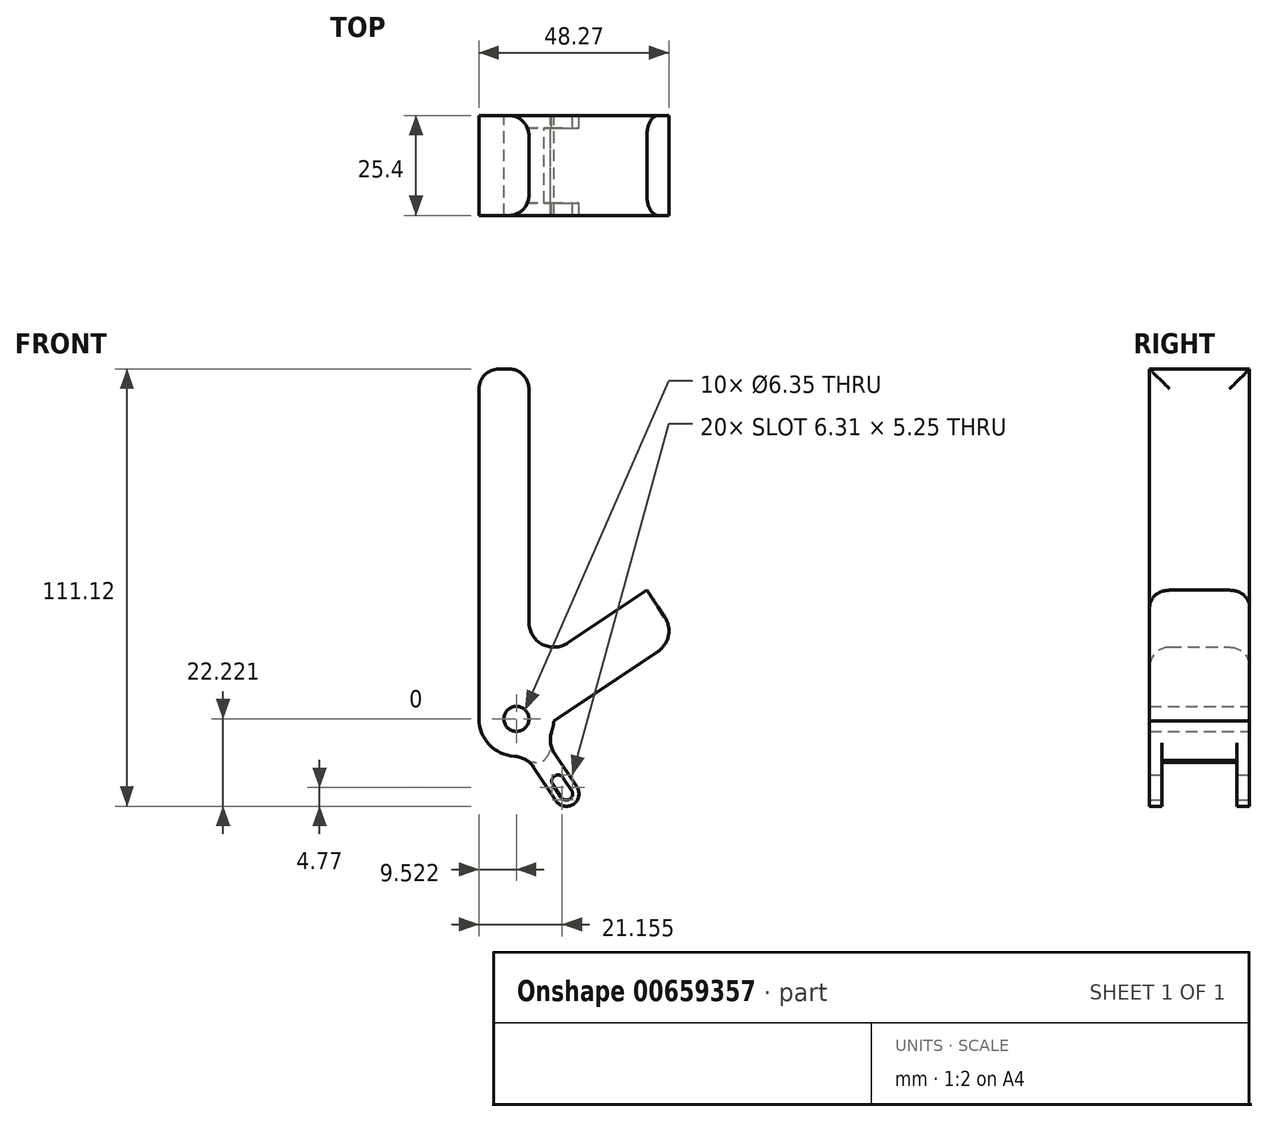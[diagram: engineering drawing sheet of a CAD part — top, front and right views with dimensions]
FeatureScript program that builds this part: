
annotation { "Feature Type Name" : "Feature", "Feature Type Description" : "" }
export const myFeature = defineFeature(function(context is Context, id is Id, definition is map)
    precondition{}
    {
        {
            var Q0;
            Q0=qCreatedBy(makeId("Front.planeOp"),FACE);
            var sketch = newSketch(context, id + "F0", { "sketchPlane" : qUnion([Q0])});
            skPoint(sketch, "E0.centerSnap0", {"position": v(3.9, -22.32) * mm});
            skArc(sketch, "E1", {"start": v(-1.4, -6.47) * mm, "mid": v(-1.04, -5.16) * mm, "end": v(-0.87, -3.81) * mm});
            skArc(sketch, "E2", {"start": v(1, -23.23) * mm, "mid": v(3.2, -23.67) * mm, "end": v(3.64, -21.47) * mm});
            skArc(sketch, "E3", {"start": v(-0.32, -24.11) * mm, "mid": v(4.08, -25) * mm, "end": v(4.96, -20.59) * mm});
            skLineSegment(sketch, "E4", {"start": v(-10.38, -3.3) * mm, "end": v(2.32, -22.35) * mm, "construction": true});
            skArc(sketch, "E5", {"start": v(1.5, -18.27) * mm, "mid": v(-0.7, -17.83) * mm, "end": v(-1.13, -20.03) * mm});
            skLineSegment(sketch, "E6", {"start": v(0.19, -19.15) * mm, "end": v(-1.13, -20.03) * mm, "construction": true});
            skLineSegment(sketch, "E7", {"start": v(0.19, -19.15) * mm, "end": v(1.5, -18.27) * mm, "construction": true});
            skLineSegment(sketch, "E8", {"start": v(1.5, -18.27) * mm, "end": v(3.64, -21.47) * mm});
            skLineSegment(sketch, "E9", {"start": v(-1.13, -20.03) * mm, "end": v(1, -23.23) * mm});
            skLineSegment(sketch, "E10", {"start": v(-10.38, -3.3) * mm, "end": v(-13.02, -5.06) * mm, "construction": true});
            skLineSegment(sketch, "E11", {"start": v(-10.38, -3.3) * mm, "end": v(-7.74, -1.54) * mm, "construction": true});
            skLineSegment(sketch, "E12", {"start": v(-0.7, -12.1) * mm, "end": v(4.96, -20.59) * mm});
            skLineSegment(sketch, "E13", {"start": v(-5.98, -15.63) * mm, "end": v(-0.32, -24.11) * mm});
            skPoint(sketch, "E14.visualSharp", {"position": v(-8.04, -12.53) * mm});
            skArc(sketch, "E14.filletArc", {"start": v(-5.98, -15.63) * mm, "mid": v(-8.1, -13.64) * mm, "end": v(-10.9, -12.8) * mm});
            skPoint(sketch, "E15.visualSharp", {"position": v(-2.75, -9.01) * mm});
            skArc(sketch, "E15.filletArc", {"start": v(-1.4, -6.47) * mm, "mid": v(-1.7, -9.37) * mm, "end": v(-0.7, -12.1) * mm});
            skLineSegment(sketch, "E16", {"start": v(-10.38, -3.3) * mm, "end": v(-16.73, -22.35) * mm, "construction": true});
            skLineSegment(sketch, "E17", {"start": v(-10.38, -3.3) * mm, "end": v(35.52, -3.3) * mm, "construction": true});
            skLineSegment(sketch, "E18", {"start": v(-10.38, -3.3) * mm, "end": v(17.5, 32.54) * mm, "construction": true});
            skLineSegment(sketch, "E19", {"start": v(-10.38, -3.3) * mm, "end": v(-10.38, -22.35) * mm, "construction": true});
            skLineSegment(sketch, "E20", {"start": v(-10.38, -3.3) * mm, "end": v(28.15, 22.39) * mm, "construction": true});
            skLineSegment(sketch, "E21", {"start": v(-0.87, -3.81) * mm, "end": v(25.54, 13.8) * mm});
            skLineSegment(sketch, "E22", {"start": v(-19.9, -3.3) * mm, "end": v(-19.9, 85.6) * mm});
            skLineSegment(sketch, "E23", {"start": v(-19.9, 85.6) * mm, "end": v(-7.2, 85.6) * mm});
            skLineSegment(sketch, "E24", {"start": v(-7.2, 85.6) * mm, "end": v(-7.2, 21.27) * mm});
            skLineSegment(sketch, "E25", {"start": v(27.3, 22.6) * mm, "end": v(22.78, 29.39) * mm});
            skLineSegment(sketch, "E26", {"start": v(2.67, 15.98) * mm, "end": v(22.78, 29.39) * mm});
            skPoint(sketch, "E27.visualSharp", {"position": v(-7.2, 9.4) * mm});
            skArc(sketch, "E27.filletArc", {"start": v(-7.2, 21.27) * mm, "mid": v(-3.85, 15.67) * mm, "end": v(2.67, 15.98) * mm});
            skPoint(sketch, "E28.visualSharp", {"position": v(30.83, 17.32) * mm});
            skArc(sketch, "E28.filletArc", {"start": v(25.54, 13.8) * mm, "mid": v(28.25, 17.83) * mm, "end": v(27.3, 22.6) * mm});
            skPoint(sketch, "E29.orphan", {"position": v(-7.22, -8.04) * mm});
            skArc(sketch, "E30.trimOffspring", {"start": v(-19.9, -3.3) * mm, "mid": v(-17.3, -9.85) * mm, "end": v(-10.9, -12.8) * mm});
            skCircle(sketch, "E31", {"center": v(-10.38, -3.3) * mm, "radius": 3.18 * mm});
            skSolve(sketch);
        }
        {
            var Q0;
            Q0 = qSketchRegion(id + "F0", true);
            extrude(context, id + "F1", {"entities" : qUnion([Q0]), "depth" : 25.4 * mm, "offsetDistance" : 25.4 * mm});
        }
        {
            var Q0;
            Q0=makeQuery(id+"F1.opExtrude","CAP_EDGE",EDGE,{"disambiguationData":[OSD([sQuery(id+"F0.wireOp",EDGE,"E24")])],"isStart":false});
            var Q1;
            Q1=makeQuery(id+"F1.opExtrude","CAP_EDGE",EDGE,{"disambiguationData":[OSD([sQuery(id+"F0.wireOp",EDGE,"E24")])],"isStart":true});
            var Q2;
            Q2=makeQuery(id+"F1.opExtrude","SWEPT_EDGE",EDGE,{"disambiguationData":[OSD([sQuery(id+"F0.wireOp",EDGE,"E23"),sQuery(id+"F0.wireOp",EDGE,"E24")])]});
            var Q3;
            Q3=makeQuery(id+"F1.opExtrude","SWEPT_EDGE",EDGE,{"disambiguationData":[OSD([sQuery(id+"F0.wireOp",EDGE,"E22"),sQuery(id+"F0.wireOp",EDGE,"E23")])]});
            fillet(context, id + "F2", {"entities" : qUnion([Q0, Q1, Q2, Q3]), "radius" : 5.08 * mm, "tangentPropagation" : true, "allowEdgeOverflow" : false});
        }
        {
            var Q0;
            Q0=makeQuery(id+"F1.opExtrude","SWEPT_FACE",FACE,{"disambiguationData":[OSD([sQuery(id+"F0.wireOp",EDGE,"E12")])]});
            var sketch = newSketch(context, id + "F3", { "sketchPlane" : qUnion([Q0])});
            skLineSegment(sketch, "E32.bottom", {"start": v(-22.23, -9.69) * mm, "end": v(-3.18, -9.69) * mm});
            skLineSegment(sketch, "E32.top", {"start": v(-22.23, -25.45) * mm, "end": v(-3.18, -25.45) * mm});
            skLineSegment(sketch, "E32.left", {"start": v(-22.23, -9.69) * mm, "end": v(-22.23, -25.45) * mm});
            skLineSegment(sketch, "E32.right", {"start": v(-3.18, -9.69) * mm, "end": v(-3.18, -25.45) * mm});
            skSolve(sketch);
        }
        {
            var Q0;
            Q0 = qSketchRegion(id + "F3", true);
            var Q1;
            Q1=makeQuery(id+"F1.opExtrude","SWEPT_FACE",FACE,{"disambiguationData":[OSD([sQuery(id+"F0.wireOp",EDGE,"E13")])]});
            extrude(context, id + "F4", {"entities" : qUnion([Q0]), "operationType" : NewBodyOperationType.REMOVE, "endBound" : BoundingType.UP_TO_SURFACE, "oppositeDirection" : true, "depth" : 25.4 * mm, "endBoundEntityFace" : qUnion([Q1]), "offsetDistance" : 25.4 * mm});
        }
        {
            var Q0;
            Q0=makeQuery(id+"F4.boolean.opBoolean","MERGE",EDGE,{"derivedFrom":[makeQuery(id+"F1.opExtrude","SWEPT_EDGE",EDGE,{"disambiguationData":[OSD([sQuery(id+"F0.wireOp",EDGE,"E12"),sQuery(id+"F0.wireOp",EDGE,"E15.filletArc")])]}),makeQuery(id+"F4.opExtrude","CAP_EDGE",EDGE,{"disambiguationData":[OSD([sQuery(id+"F3.wireOp",EDGE,"E32.bottom")])],"isStart":true})]});
            var Q1;
            {var subQ0=sQuery(id+"F0.wireOp",EDGE,"E13");Q1=makeQuery(id+"F4.boolean.opBoolean","MERGE",EDGE,{"derivedFrom":[makeQuery(id+"F1.opExtrude","SWEPT_EDGE",EDGE,{"disambiguationData":[OSD([subQ0,sQuery(id+"F0.wireOp",EDGE,"E14.filletArc")])]}),makeQuery(id+"F4.opExtrude","TWEAK_EDGE",EDGE,{"derivedFrom":[makeQuery(id+"F1.opExtrude","SWEPT_FACE",FACE,{"disambiguationData":[OSD([subQ0])]}),makeQuery(id+"F3.imprint","IMPRINT",EDGE,{"derivedFrom":sQuery(id+"F3.wireOp",EDGE,"E32.bottom")})]})]});}
            fillet(context, id + "F5", {"entities" : qUnion([Q0, Q1]), "radius" : 5.08 * mm, "tangentPropagation" : true, "allowEdgeOverflow" : false});
        }
    });
